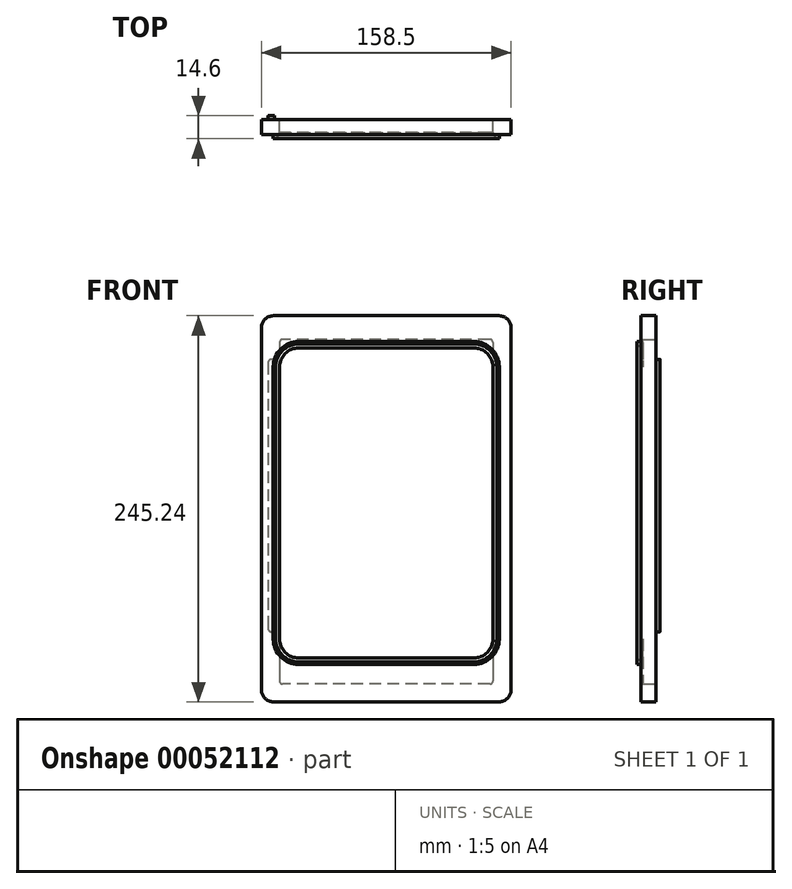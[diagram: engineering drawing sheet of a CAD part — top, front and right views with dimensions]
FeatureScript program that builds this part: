
annotation { "Feature Type Name" : "Feature", "Feature Type Description" : "" }
export const myFeature = defineFeature(function(context is Context, id is Id, definition is map)
    precondition{}
    {
        {
            var Q0;
            Q0=qCreatedBy(makeId("Front.planeOp"),FACE);
            var sketch = newSketch(context, id + "F0", { "sketchPlane" : qUnion([Q0])});
            skLineSegment(sketch, "E0.bottom", {"start": v(-71.63, 122.63) * mm, "end": v(71.63, 122.62) * mm});
            skLineSegment(sketch, "E0.top", {"start": v(-71.63, -122.62) * mm, "end": v(71.63, -122.63) * mm});
            skLineSegment(sketch, "E0.left", {"start": v(-79.25, 115) * mm, "end": v(-79.25, -115) * mm});
            skLineSegment(sketch, "E0.right", {"start": v(79.25, 115) * mm, "end": v(79.25, -115) * mm});
            skLineSegment(sketch, "E1", {"start": v(0, 122.63) * mm, "end": v(0, 0) * mm, "construction": true});
            skLineSegment(sketch, "E2", {"start": v(0, 0) * mm, "end": v(0, -122.63) * mm, "construction": true});
            skLineSegment(sketch, "E3", {"start": v(-79.25, 0) * mm, "end": v(0, 0) * mm, "construction": true});
            skLineSegment(sketch, "E4", {"start": v(79.25, 0) * mm, "end": v(0, 0) * mm, "construction": true});
            skPoint(sketch, "E5.visualSharp", {"position": v(-79.25, 122.62) * mm});
            skArc(sketch, "E5.filletArc", {"start": v(-71.63, 122.63) * mm, "mid": v(-77.02, 120.4) * mm, "end": v(-79.25, 115) * mm});
            skPoint(sketch, "E6.visualSharp", {"position": v(79.25, 122.62) * mm});
            skArc(sketch, "E6.filletArc", {"start": v(79.25, 115) * mm, "mid": v(77.02, 120.4) * mm, "end": v(71.63, 122.63) * mm});
            skPoint(sketch, "E7.visualSharp", {"position": v(-79.25, -122.63) * mm});
            skArc(sketch, "E7.filletArc", {"start": v(-79.25, -115) * mm, "mid": v(-77.02, -120.4) * mm, "end": v(-71.63, -122.63) * mm});
            skPoint(sketch, "E8.visualSharp", {"position": v(79.25, -122.63) * mm});
            skArc(sketch, "E8.filletArc", {"start": v(71.63, -122.63) * mm, "mid": v(77.02, -120.4) * mm, "end": v(79.25, -115) * mm});
            skSolve(sketch);
        }
        {
            var Q0;
            Q0=makeQuery(id+"F0.imprint","IMPRINT",FACE,{"disambiguationData":[TD([[makeQuery(id+"F0.imprint","IMPRINT",EDGE,{"derivedFrom":sQuery(id+"F0.wireOp",EDGE,"E0.bottom")}),-1.0]])]});
            extrude(context, id + "F1", {"entities" : qUnion([Q0]), "oppositeDirection" : true, "depth" : 9.6 * mm});
        }
        {
            var Q0;
            Q0=makeQuery(id+"F0.imprint","IMPRINT",FACE,{"disambiguationData":[TD([[makeQuery(id+"F0.imprint","IMPRINT",EDGE,{"derivedFrom":sQuery(id+"F0.wireOp",EDGE,"E0.bottom")}),-1.0]])]});
            var sketch = newSketch(context, id + "F2", { "sketchPlane" : qUnion([Q0])});
            skLineSegment(sketch, "E9.bottom", {"start": v(-55.6, 102.2) * mm, "end": v(55.6, 102.2) * mm});
            skLineSegment(sketch, "E9.top", {"start": v(-55.6, -94.8) * mm, "end": v(55.6, -94.8) * mm});
            skLineSegment(sketch, "E9.left", {"start": v(-67.75, 90.06) * mm, "end": v(-67.75, -82.65) * mm});
            skLineSegment(sketch, "E9.right", {"start": v(67.75, 90.06) * mm, "end": v(67.75, -82.65) * mm});
            skLineSegment(sketch, "E10", {"start": v(0, 102.2) * mm, "end": v(0, 0) * mm, "construction": true});
            skLineSegment(sketch, "E11", {"start": v(0, 0) * mm, "end": v(0, -94.8) * mm, "construction": true});
            skPoint(sketch, "E12.visualSharp", {"position": v(-67.75, 102.2) * mm});
            skArc(sketch, "E12.filletArc", {"start": v(-55.6, 102.2) * mm, "mid": v(-64.2, 98.65) * mm, "end": v(-67.75, 90.06) * mm});
            skPoint(sketch, "E13.visualSharp", {"position": v(67.75, 102.2) * mm});
            skArc(sketch, "E13.filletArc", {"start": v(67.75, 90.06) * mm, "mid": v(64.2, 98.65) * mm, "end": v(55.6, 102.2) * mm});
            skPoint(sketch, "E14.visualSharp", {"position": v(67.75, -94.8) * mm});
            skArc(sketch, "E14.filletArc", {"start": v(55.6, -94.8) * mm, "mid": v(64.2, -91.24) * mm, "end": v(67.75, -82.65) * mm});
            skPoint(sketch, "E15.visualSharp", {"position": v(-67.75, -94.8) * mm});
            skArc(sketch, "E15.filletArc", {"start": v(-67.75, -82.65) * mm, "mid": v(-64.2, -91.24) * mm, "end": v(-55.6, -94.8) * mm});
            skLineSegment(sketch, "E16", {"start": v(-67.75, 3.98) * mm, "end": v(0, 3.98) * mm, "construction": true});
            skLineSegment(sketch, "E17", {"start": v(0, 3.98) * mm, "end": v(67.75, 3.98) * mm, "construction": true});
            skLineSegment(sketch, "E18", {"start": v(0, 122.62) * mm, "end": v(0, 102.2) * mm, "construction": true});
            skLineSegment(sketch, "E19", {"start": v(-67.75, 3.98) * mm, "end": v(-79.25, 3.98) * mm, "construction": true});
            skLineSegment(sketch, "E20", {"start": v(67.75, 3.98) * mm, "end": v(79.25, 3.98) * mm, "construction": true});
            skSolve(sketch);
        }
        {
            var Q0;
            Q0 = qSketchRegion(id + "F2", true);
            extrude(context, id + "F3", {"entities" : qUnion([Q0]), "operationType" : NewBodyOperationType.REMOVE, "oppositeDirection" : true, "depth" : 10 * mm});
        }
        {
            var Q0;
            Q0=makeQuery(id+"F1.opExtrude","CAP_FACE",FACE,{"disambiguationData":[OSD([sQuery(id+"F0.wireOp",EDGE,"E0.bottom"),sQuery(id+"F0.wireOp",EDGE,"E0.top"),sQuery(id+"F0.wireOp",EDGE,"E0.left"),sQuery(id+"F0.wireOp",EDGE,"E0.right"),sQuery(id+"F0.wireOp",EDGE,"E5.filletArc"),sQuery(id+"F0.wireOp",EDGE,"E6.filletArc"),sQuery(id+"F0.wireOp",EDGE,"E7.filletArc"),sQuery(id+"F0.wireOp",EDGE,"E8.filletArc")])],"isStart":true});
            var sketch = newSketch(context, id + "F4", { "sketchPlane" : qUnion([Q0])});
            skLineSegment(sketch, "E21.bottom", {"start": v(-55.6, 106.25) * mm, "end": v(55.6, 106.25) * mm});
            skLineSegment(sketch, "E21.top", {"start": v(-55.6, -98.85) * mm, "end": v(55.6, -98.85) * mm});
            skLineSegment(sketch, "E21.left", {"start": v(-71.8, 90.06) * mm, "end": v(-71.8, -82.65) * mm});
            skLineSegment(sketch, "E21.right", {"start": v(71.8, 90.06) * mm, "end": v(71.8, -82.65) * mm});
            skLineSegment(sketch, "E22", {"start": v(0, 102.2) * mm, "end": v(0, 106.25) * mm, "construction": true});
            skLineSegment(sketch, "E23", {"start": v(67.75, 0) * mm, "end": v(71.8, 0) * mm, "construction": true});
            skLineSegment(sketch, "E24", {"start": v(-67.75, 0) * mm, "end": v(-71.8, 0) * mm, "construction": true});
            skLineSegment(sketch, "E25", {"start": v(0, -94.8) * mm, "end": v(0, -98.85) * mm, "construction": true});
            skPoint(sketch, "E26.visualSharp", {"position": v(-71.8, 106.25) * mm});
            skArc(sketch, "E26.filletArc", {"start": v(-55.6, 106.26) * mm, "mid": v(-67.06, 101.51) * mm, "end": v(-71.8, 90.06) * mm});
            skPoint(sketch, "E27.visualSharp", {"position": v(71.8, 106.25) * mm});
            skArc(sketch, "E27.filletArc", {"start": v(71.8, 90.06) * mm, "mid": v(67.06, 101.51) * mm, "end": v(55.6, 106.25) * mm});
            skPoint(sketch, "E28.visualSharp", {"position": v(71.8, -98.85) * mm});
            skArc(sketch, "E28.filletArc", {"start": v(55.6, -98.85) * mm, "mid": v(67.06, -94.1) * mm, "end": v(71.8, -82.65) * mm});
            skPoint(sketch, "E29.visualSharp", {"position": v(-71.8, -98.85) * mm});
            skArc(sketch, "E29.filletArc", {"start": v(-71.8, -82.65) * mm, "mid": v(-67.06, -94.1) * mm, "end": v(-55.6, -98.85) * mm});
            skSolve(sketch);
        }
        {
            var Q0;
            Q0 = qSketchRegion(id + "F4", true);
            extrude(context, id + "F5", {"entities" : qUnion([Q0]), "operationType" : NewBodyOperationType.ADD, "depth" : 2.5 * mm});
        }
        {
            var Q0;
            Q0 = qSketchRegion(id + "F2", true);
            extrude(context, id + "F6", {"entities" : qUnion([Q0]), "operationType" : NewBodyOperationType.REMOVE, "depth" : 68.83 * mm});
        }
        {
            var Q0;
            Q0=makeQuery(id+"F6.boolean.opBoolean","INTERSECT",EDGE,{"derivedFrom":[makeQuery(id+"F5.opExtrude","CAP_FACE",FACE,{"disambiguationData":[OSD([sQuery(id+"F4.wireOp",EDGE,"E21.bottom"),sQuery(id+"F4.wireOp",EDGE,"E21.top"),sQuery(id+"F4.wireOp",EDGE,"E21.left"),sQuery(id+"F4.wireOp",EDGE,"E21.right"),sQuery(id+"F4.wireOp",EDGE,"E26.filletArc"),sQuery(id+"F4.wireOp",EDGE,"E27.filletArc"),sQuery(id+"F4.wireOp",EDGE,"E28.filletArc"),sQuery(id+"F4.wireOp",EDGE,"E29.filletArc")])],"isStart":false}),makeQuery(id+"F6.opExtrude","SWEPT_FACE",FACE,{"disambiguationData":[OSD([sQuery(id+"F2.wireOp",EDGE,"E9.right")])]})]});
            chamfer(context, id + "F7", {"entities" : qUnion([Q0]), "width" : 2.5 * mm, "tangentPropagation" : true});
        }
        {
            var Q0;
            Q0=makeQuery(id+"F1.opExtrude","CAP_FACE",FACE,{"disambiguationData":[OSD([sQuery(id+"F0.wireOp",EDGE,"E0.bottom"),sQuery(id+"F0.wireOp",EDGE,"E0.top"),sQuery(id+"F0.wireOp",EDGE,"E0.left"),sQuery(id+"F0.wireOp",EDGE,"E0.right"),sQuery(id+"F0.wireOp",EDGE,"E5.filletArc"),sQuery(id+"F0.wireOp",EDGE,"E6.filletArc"),sQuery(id+"F0.wireOp",EDGE,"E7.filletArc"),sQuery(id+"F0.wireOp",EDGE,"E8.filletArc")])],"isStart":false});
            var sketch = newSketch(context, id + "F8", { "sketchPlane" : qUnion([Q0])});
            skLineSegment(sketch, "E30.bottom", {"start": v(-65.75, 107.62) * mm, "end": v(65.75, 107.62) * mm});
            skLineSegment(sketch, "E30.top", {"start": v(-65.75, -111.38) * mm, "end": v(65.75, -111.38) * mm});
            skLineSegment(sketch, "E30.left", {"start": v(-67.75, 105.62) * mm, "end": v(-67.75, -109.38) * mm});
            skLineSegment(sketch, "E30.right", {"start": v(67.75, 105.62) * mm, "end": v(67.75, -109.38) * mm});
            skLineSegment(sketch, "E31", {"start": v(0, 107.62) * mm, "end": v(0, 102.2) * mm, "construction": true});
            skLineSegment(sketch, "E32", {"start": v(-67.75, 0) * mm, "end": v(0, 0) * mm, "construction": true});
            skLineSegment(sketch, "E33", {"start": v(0, 0) * mm, "end": v(67.75, 0) * mm, "construction": true});
            skPoint(sketch, "E34.visualSharp", {"position": v(-67.75, 107.62) * mm});
            skArc(sketch, "E34.filletArc", {"start": v(-65.75, 107.62) * mm, "mid": v(-67.16, 107.04) * mm, "end": v(-67.75, 105.62) * mm});
            skPoint(sketch, "E35.visualSharp", {"position": v(67.75, 107.62) * mm});
            skArc(sketch, "E35.filletArc", {"start": v(67.75, 105.62) * mm, "mid": v(67.16, 107.04) * mm, "end": v(65.75, 107.63) * mm});
            skPoint(sketch, "E36.visualSharp", {"position": v(67.75, -111.38) * mm});
            skArc(sketch, "E36.filletArc", {"start": v(65.75, -111.38) * mm, "mid": v(67.16, -110.79) * mm, "end": v(67.75, -109.38) * mm});
            skPoint(sketch, "E37.visualSharp", {"position": v(-67.75, -111.38) * mm});
            skArc(sketch, "E37.filletArc", {"start": v(-67.75, -109.38) * mm, "mid": v(-67.16, -110.79) * mm, "end": v(-65.75, -111.38) * mm});
            skLineSegment(sketch, "E38", {"start": v(0, 107.62) * mm, "end": v(0, 122.62) * mm, "construction": true});
            skSolve(sketch);
        }
        {
            var Q0;
            Q0 = qSketchRegion(id + "F8", true);
            extrude(context, id + "F9", {"entities" : qUnion([Q0]), "operationType" : NewBodyOperationType.REMOVE, "oppositeDirection" : true, "depth" : 8.2 * mm});
        }
        {
            var Q0;
            Q0=makeQuery(id+"F1.opExtrude","CAP_FACE",FACE,{"disambiguationData":[OSD([sQuery(id+"F0.wireOp",EDGE,"E0.bottom"),sQuery(id+"F0.wireOp",EDGE,"E0.top"),sQuery(id+"F0.wireOp",EDGE,"E0.left"),sQuery(id+"F0.wireOp",EDGE,"E0.right"),sQuery(id+"F0.wireOp",EDGE,"E5.filletArc"),sQuery(id+"F0.wireOp",EDGE,"E6.filletArc"),sQuery(id+"F0.wireOp",EDGE,"E7.filletArc"),sQuery(id+"F0.wireOp",EDGE,"E8.filletArc")])],"isStart":false});
            var sketch = newSketch(context, id + "F10", { "sketchPlane" : qUnion([Q0])});
            skLineSegment(sketch, "E39.bottom", {"start": v(73, 94.88) * mm, "end": v(73.05, 94.88) * mm});
            skLineSegment(sketch, "E39.top", {"start": v(73, -78.12) * mm, "end": v(73.05, -78.12) * mm});
            skLineSegment(sketch, "E39.left", {"start": v(71, 92.88) * mm, "end": v(71, -76.12) * mm});
            skLineSegment(sketch, "E39.right", {"start": v(75.05, 92.88) * mm, "end": v(75.05, -76.12) * mm});
            skLineSegment(sketch, "E40", {"start": v(75.05, 0) * mm, "end": v(79.25, 0) * mm, "construction": true});
            skPoint(sketch, "E41.visualSharp", {"position": v(71, 94.88) * mm});
            skArc(sketch, "E41.filletArc", {"start": v(73, 94.88) * mm, "mid": v(71.59, 94.29) * mm, "end": v(71, 92.88) * mm});
            skPoint(sketch, "E42.visualSharp", {"position": v(75.05, 94.88) * mm});
            skArc(sketch, "E42.filletArc", {"start": v(75.05, 92.88) * mm, "mid": v(74.46, 94.29) * mm, "end": v(73.05, 94.88) * mm});
            skPoint(sketch, "E43.visualSharp", {"position": v(75.05, -78.12) * mm});
            skArc(sketch, "E43.filletArc", {"start": v(73.05, -78.12) * mm, "mid": v(74.46, -77.54) * mm, "end": v(75.05, -76.12) * mm});
            skPoint(sketch, "E44.visualSharp", {"position": v(71, -78.12) * mm});
            skArc(sketch, "E44.filletArc", {"start": v(71, -76.12) * mm, "mid": v(71.59, -77.54) * mm, "end": v(73, -78.12) * mm});
            skSolve(sketch);
        }
        {
            var Q0;
            Q0 = qSketchRegion(id + "F10", true);
            extrude(context, id + "F11", {"entities" : qUnion([Q0]), "operationType" : NewBodyOperationType.ADD, "depth" : 2.5 * mm});
        }
    });
